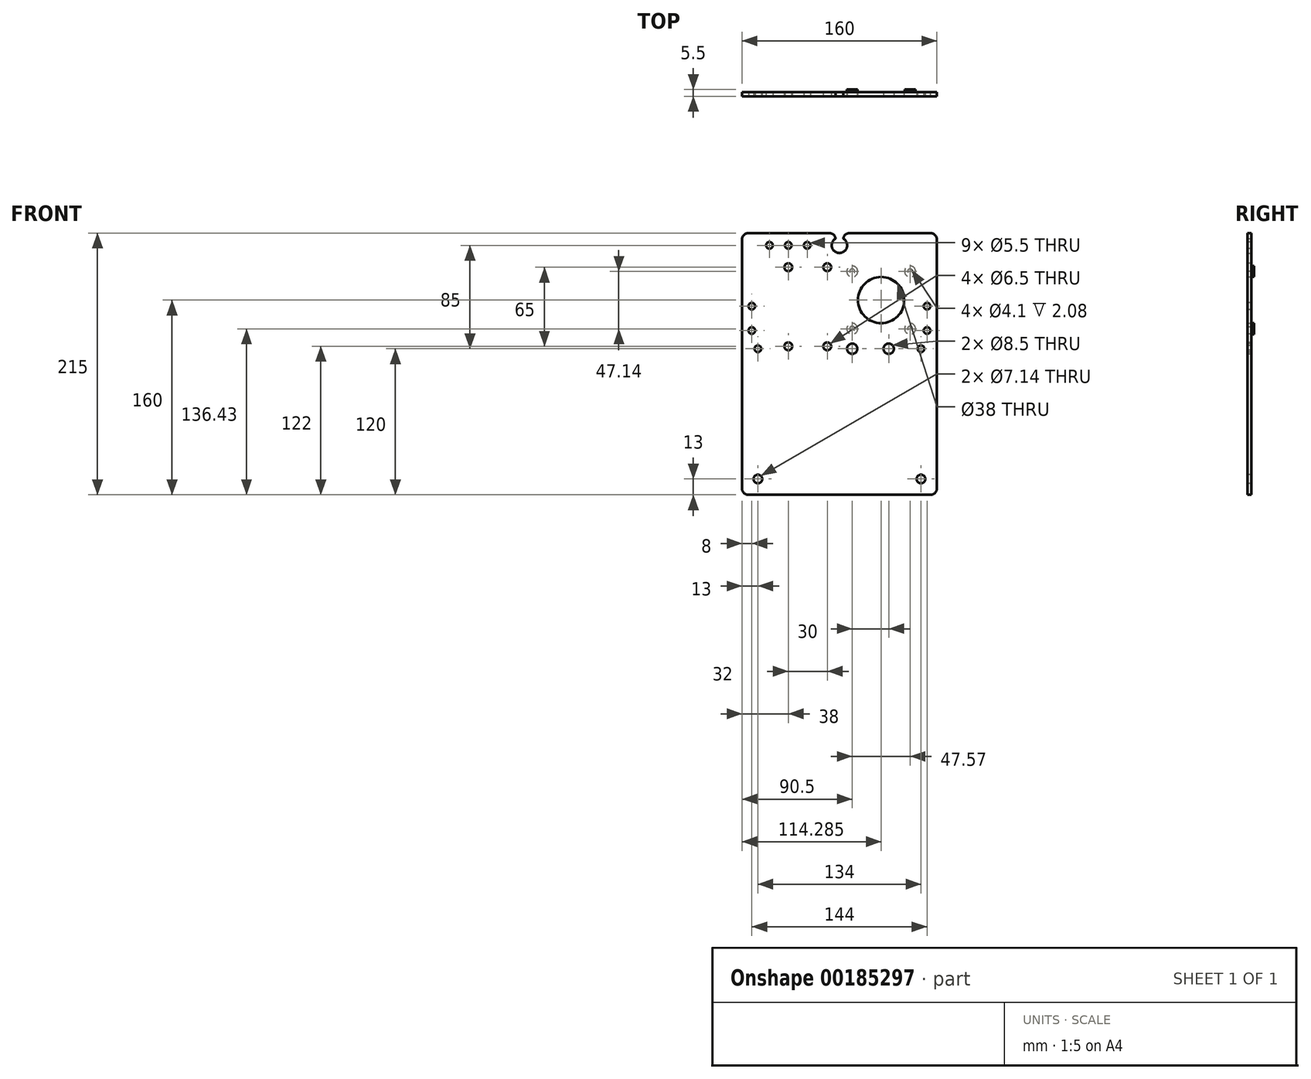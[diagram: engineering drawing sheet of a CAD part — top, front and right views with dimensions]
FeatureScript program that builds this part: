
annotation { "Feature Type Name" : "Feature", "Feature Type Description" : "" }
export const myFeature = defineFeature(function(context is Context, id is Id, definition is map)
    precondition{}
    {
        {
            var Q0;
            Q0=qCreatedBy(makeId("Front.planeOp"),FACE);
            var sketch = newSketch(context, id + "F0", { "sketchPlane" : qUnion([Q0])});
            skLineSegment(sketch, "E0.top", {"start": v(80, -107.5) * mm, "end": v(-80, -107.5) * mm});
            skLineSegment(sketch, "E0.right", {"start": v(-80, 107.5) * mm, "end": v(-80, -107.5) * mm});
            skPoint(sketch, "E0.middle", {"position": v(0, 0) * mm});
            skLineSegment(sketch, "E1", {"start": v(-80, 107.5) * mm, "end": v(-3.18, 107.5) * mm});
            skLineSegment(sketch, "E2", {"start": v(-3.18, 107.5) * mm, "end": v(-3.18, 103) * mm});
            skLineSegment(sketch, "E3", {"start": v(3.17, 103) * mm, "end": v(3.17, 107.5) * mm});
            skLineSegment(sketch, "E4", {"start": v(3.17, 107.5) * mm, "end": v(80, 107.5) * mm});
            skLineSegment(sketch, "E5", {"start": v(80, 107.5) * mm, "end": v(80, -107.5) * mm});
            skArc(sketch, "E6", {"start": v(-3.18, 103) * mm, "mid": v(0, 91.15) * mm, "end": v(3.17, 103) * mm});
            skLineSegment(sketch, "E7", {"start": v(7.75, 80.07) * mm, "end": v(7.75, 72.07) * mm, "construction": true});
            skLineSegment(sketch, "E8", {"start": v(13.25, 72.07) * mm, "end": v(13.25, 80.07) * mm, "construction": true});
            skLineSegment(sketch, "E9", {"start": v(55.32, 80.07) * mm, "end": v(55.32, 72.07) * mm, "construction": true});
            skLineSegment(sketch, "E10", {"start": v(60.82, 72.07) * mm, "end": v(60.82, 80.07) * mm, "construction": true});
            skLineSegment(sketch, "E11", {"start": v(60.82, 24.93) * mm, "end": v(60.82, 32.93) * mm, "construction": true});
            skLineSegment(sketch, "E12", {"start": v(55.32, 32.93) * mm, "end": v(55.32, 24.93) * mm, "construction": true});
            skLineSegment(sketch, "E13", {"start": v(13.25, 24.93) * mm, "end": v(13.25, 32.93) * mm, "construction": true});
            skLineSegment(sketch, "E14", {"start": v(7.75, 32.93) * mm, "end": v(7.75, 24.93) * mm, "construction": true});
            skLineSegment(sketch, "E15", {"start": v(7.75, 76.07) * mm, "end": v(13.25, 76.07) * mm, "construction": true});
            skLineSegment(sketch, "E16", {"start": v(55.32, 76.07) * mm, "end": v(60.82, 76.07) * mm, "construction": true});
            skLineSegment(sketch, "E17", {"start": v(55.32, 28.93) * mm, "end": v(60.82, 28.93) * mm, "construction": true});
            skLineSegment(sketch, "E18", {"start": v(13.25, 28.93) * mm, "end": v(7.75, 28.93) * mm, "construction": true});
            skPoint(sketch, "E18.endSnap0", {"position": v(7.75, 28.93) * mm});
            skLineSegment(sketch, "E19", {"start": v(10.5, 76.07) * mm, "end": v(10.5, 28.93) * mm, "construction": true});
            skLineSegment(sketch, "E20", {"start": v(10.5, 28.93) * mm, "end": v(58.07, 28.93) * mm, "construction": true});
            skLineSegment(sketch, "E21", {"start": v(58.07, 28.93) * mm, "end": v(58.07, 76.07) * mm, "construction": true});
            skLineSegment(sketch, "E22", {"start": v(58.07, 76.07) * mm, "end": v(10.5, 76.07) * mm, "construction": true});
            skArc(sketch, "E23", {"start": v(7.75, 80.07) * mm, "mid": v(10.5, 82.82) * mm, "end": v(13.25, 80.07) * mm, "construction": true});
            skArc(sketch, "E24", {"start": v(7.75, 72.07) * mm, "mid": v(10.5, 69.32) * mm, "end": v(13.25, 72.07) * mm, "construction": true});
            skArc(sketch, "E25", {"start": v(55.32, 80.07) * mm, "mid": v(58.07, 82.82) * mm, "end": v(60.82, 80.07) * mm, "construction": true});
            skArc(sketch, "E26", {"start": v(55.32, 72.07) * mm, "mid": v(58.07, 69.32) * mm, "end": v(60.82, 72.07) * mm, "construction": true});
            skArc(sketch, "E27", {"start": v(7.75, 32.93) * mm, "mid": v(10.5, 35.68) * mm, "end": v(13.25, 32.93) * mm, "construction": true});
            skArc(sketch, "E28", {"start": v(7.75, 24.93) * mm, "mid": v(10.5, 22.18) * mm, "end": v(13.25, 24.93) * mm, "construction": true});
            skArc(sketch, "E29", {"start": v(55.32, 32.93) * mm, "mid": v(58.07, 35.68) * mm, "end": v(60.82, 32.93) * mm, "construction": true});
            skArc(sketch, "E30", {"start": v(55.32, 24.93) * mm, "mid": v(58.07, 22.18) * mm, "end": v(60.82, 24.93) * mm, "construction": true});
            skCircle(sketch, "E31", {"center": v(34.29, 52.5) * mm, "radius": 19 * mm});
            skLineSegment(sketch, "E32", {"start": v(10.5, 52.5) * mm, "end": v(34.29, 52.5) * mm, "construction": true});
            skLineSegment(sketch, "E33", {"start": v(34.28, 52.5) * mm, "end": v(34.28, 76.07) * mm, "construction": true});
            skSolve(sketch);
        }
        {
            var Q0;
            Q0 = qSketchRegion(id + "F0", true);
            extrude(context, id + "F1", {"entities" : qUnion([Q0]), "depth" : 3.42 * mm});
        }
        {
            var Q0;
            Q0=makeQuery(id+"F1.opExtrude","SWEPT_EDGE",EDGE,{"disambiguationData":[OSD([sQuery(id+"F0.wireOp",EDGE,"E0.right"),sQuery(id+"F0.wireOp",EDGE,"E1")])]});
            var Q1;
            Q1=makeQuery(id+"F1.opExtrude","SWEPT_EDGE",EDGE,{"disambiguationData":[OSD([sQuery(id+"F0.wireOp",EDGE,"wBwmQqUi-94Xi-KIoa-cwVM-h10VN6lgfSyI"),sQuery(id+"F0.wireOp",EDGE,"E4")])]});
            var Q2;
            Q2=makeQuery(id+"F1.opExtrude","SWEPT_EDGE",EDGE,{"disambiguationData":[OSD([sQuery(id+"F0.wireOp",EDGE,"wBwmQqUi-94Xi-KIoa-cwVM-h10VN6lgfSyI"),sQuery(id+"F0.wireOp",EDGE,"zVrTCUyL-jB1j-ef0g-tJN7-1HJSPVF5DUSU")])]});
            var Q3;
            Q3=makeQuery(id+"F1.opExtrude","SWEPT_EDGE",EDGE,{"disambiguationData":[OSD([sQuery(id+"F0.wireOp",EDGE,"zVrTCUyL-jB1j-ef0g-tJN7-1HJSPVF5DUSU"),sQuery(id+"F0.wireOp",EDGE,"E5")])]});
            var Q4;
            Q4=makeQuery(id+"F1.opExtrude","SWEPT_EDGE",EDGE,{"disambiguationData":[OSD([sQuery(id+"F0.wireOp",EDGE,"E1"),sQuery(id+"F0.wireOp",EDGE,"E2")])]});
            var Q5;
            Q5=makeQuery(id+"F1.opExtrude","SWEPT_EDGE",EDGE,{"disambiguationData":[OSD([sQuery(id+"F0.wireOp",EDGE,"E3"),sQuery(id+"F0.wireOp",EDGE,"E4")])]});
            var Q6;
            Q6=makeQuery(id+"F1.opExtrude","SWEPT_EDGE",EDGE,{"disambiguationData":[OSD([sQuery(id+"F0.wireOp",EDGE,"E0.top"),sQuery(id+"F0.wireOp",EDGE,"E5")])]});
            var Q7;
            Q7=makeQuery(id+"F1.opExtrude","SWEPT_EDGE",EDGE,{"disambiguationData":[OSD([sQuery(id+"F0.wireOp",EDGE,"E0.top"),sQuery(id+"F0.wireOp",EDGE,"E0.right")])]});
            fillet(context, id + "F2", {"entities" : qUnion([Q0, Q1, Q2, Q3, Q4, Q5, Q6, Q7]), "radius" : 5 * mm, "tangentPropagation" : true, "allowEdgeOverflow" : false});
        }
        {
            var Q0;
            Q0=makeQuery(id+"F1.opExtrude","CAP_FACE",FACE,{"disambiguationData":[OSD([sQuery(id+"F0.wireOp",EDGE,"E0.top"),sQuery(id+"F0.wireOp",EDGE,"E0.right"),sQuery(id+"F0.wireOp",EDGE,"wBwmQqUi-94Xi-KIoa-cwVM-h10VN6lgfSyI"),sQuery(id+"F0.wireOp",EDGE,"zVrTCUyL-jB1j-ef0g-tJN7-1HJSPVF5DUSU"),sQuery(id+"F0.wireOp",EDGE,"E1"),sQuery(id+"F0.wireOp",EDGE,"E2"),sQuery(id+"F0.wireOp",EDGE,"E3"),sQuery(id+"F0.wireOp",EDGE,"E4"),sQuery(id+"F0.wireOp",EDGE,"E5"),sQuery(id+"F0.wireOp",EDGE,"E6"),sQuery(id+"F0.wireOp",EDGE,"E7"),sQuery(id+"F0.wireOp",EDGE,"E8"),sQuery(id+"F0.wireOp",EDGE,"E9"),sQuery(id+"F0.wireOp",EDGE,"E10"),sQuery(id+"F0.wireOp",EDGE,"E11"),sQuery(id+"F0.wireOp",EDGE,"E12"),sQuery(id+"F0.wireOp",EDGE,"E13"),sQuery(id+"F0.wireOp",EDGE,"E14"),sQuery(id+"F0.wireOp",EDGE,"E23"),sQuery(id+"F0.wireOp",EDGE,"E24"),sQuery(id+"F0.wireOp",EDGE,"E25"),sQuery(id+"F0.wireOp",EDGE,"E26"),sQuery(id+"F0.wireOp",EDGE,"E27"),sQuery(id+"F0.wireOp",EDGE,"E28"),sQuery(id+"F0.wireOp",EDGE,"E29"),sQuery(id+"F0.wireOp",EDGE,"E30")])],"isStart":false});
            var sketch = newSketch(context, id + "F3", { "sketchPlane" : qUnion([Q0])});
            skLineSegment(sketch, "E34", {"start": v(-42, 100) * mm, "end": v(-42, 95) * mm, "construction": true});
            skLineSegment(sketch, "E35", {"start": v(-57.5, 97.5) * mm, "end": v(-26.5, 97.5) * mm, "construction": true});
            skPoint(sketch, "E36", {"position": v(-42, 97.5) * mm});
            skLineSegment(sketch, "E37.bottom", {"start": v(-42, 79.5) * mm, "end": v(-10, 79.5) * mm, "construction": true});
            skLineSegment(sketch, "E37.top", {"start": v(-42, 14.5) * mm, "end": v(-10, 14.5) * mm, "construction": true});
            skLineSegment(sketch, "E37.left", {"start": v(-42, 79.5) * mm, "end": v(-42, 14.5) * mm, "construction": true});
            skLineSegment(sketch, "E37.right", {"start": v(-10, 79.5) * mm, "end": v(-10, 14.5) * mm, "construction": true});
            skLineSegment(sketch, "E38.bottom", {"start": v(-72, 47.5) * mm, "end": v(72, 47.5) * mm, "construction": true});
            skLineSegment(sketch, "E38.top", {"start": v(-72, 27.5) * mm, "end": v(72, 27.5) * mm, "construction": true});
            skLineSegment(sketch, "E38.left", {"start": v(-72, 47.5) * mm, "end": v(-72, 27.5) * mm, "construction": true});
            skLineSegment(sketch, "E38.right", {"start": v(72, 47.5) * mm, "end": v(72, 27.5) * mm, "construction": true});
            skLineSegment(sketch, "E39", {"start": v(10.5, 12.5) * mm, "end": v(40.5, 12.5) * mm, "construction": true});
            skLineSegment(sketch, "E40", {"start": v(-67, -94.5) * mm, "end": v(67, -94.5) * mm, "construction": true});
            skLineSegment(sketch, "E41", {"start": v(10.5, 12.5) * mm, "end": v(-67, 12.5) * mm, "construction": true});
            skLineSegment(sketch, "E42", {"start": v(40.5, 12.5) * mm, "end": v(67, 12.5) * mm, "construction": true});
            skLineSegment(sketch, "E43", {"start": v(67, 12.5) * mm, "end": v(67, -94.5) * mm, "construction": true});
            skSolve(sketch);
        }
        {
            var Q0;
            Q0=sQuery(id+"F3.wireOp",VERTEX,"E37.left.start");
            var Q1;
            Q1=sQuery(id+"F3.wireOp",VERTEX,"E37.right.start");
            var Q2;
            Q2=sQuery(id+"F3.wireOp",VERTEX,"E37.left.end");
            var Q3;
            Q3=sQuery(id+"F3.wireOp",VERTEX,"E37.right.end");
            var Q4;
            Q4=makeQuery(id+"F1.opExtrude","SWEPT_BODY",BODY,{"disambiguationData":[OSD([sQuery(id+"F0.wireOp",EDGE,"E0.top"),sQuery(id+"F0.wireOp",EDGE,"E0.right"),sQuery(id+"F0.wireOp",EDGE,"wBwmQqUi-94Xi-KIoa-cwVM-h10VN6lgfSyI"),sQuery(id+"F0.wireOp",EDGE,"zVrTCUyL-jB1j-ef0g-tJN7-1HJSPVF5DUSU"),sQuery(id+"F0.wireOp",EDGE,"E1"),sQuery(id+"F0.wireOp",EDGE,"E2"),sQuery(id+"F0.wireOp",EDGE,"E3"),sQuery(id+"F0.wireOp",EDGE,"E4"),sQuery(id+"F0.wireOp",EDGE,"E5"),sQuery(id+"F0.wireOp",EDGE,"E6"),sQuery(id+"F0.wireOp",EDGE,"E7"),sQuery(id+"F0.wireOp",EDGE,"E8"),sQuery(id+"F0.wireOp",EDGE,"E9"),sQuery(id+"F0.wireOp",EDGE,"E10"),sQuery(id+"F0.wireOp",EDGE,"E11"),sQuery(id+"F0.wireOp",EDGE,"E12"),sQuery(id+"F0.wireOp",EDGE,"E13"),sQuery(id+"F0.wireOp",EDGE,"E14"),sQuery(id+"F0.wireOp",EDGE,"E23"),sQuery(id+"F0.wireOp",EDGE,"E24"),sQuery(id+"F0.wireOp",EDGE,"E25"),sQuery(id+"F0.wireOp",EDGE,"E26"),sQuery(id+"F0.wireOp",EDGE,"E27"),sQuery(id+"F0.wireOp",EDGE,"E28"),sQuery(id+"F0.wireOp",EDGE,"E29"),sQuery(id+"F0.wireOp",EDGE,"E30")])]});
            hole(context, id + "F4", {"style" : HoleStyle.SIMPLE, "endStyle" : HoleEndStyle.THROUGH, "holeDiameter" : 6.5 * mm, "locations" : qUnion([Q0, Q1, Q2, Q3]), "scope" : qUnion([Q4]), "isTappedThrough" : true});
        }
        {
            var Q0;
            Q0=sQuery(id+"F3.wireOp",VERTEX,"E38.bottom.start");
            var Q1;
            Q1=sQuery(id+"F3.wireOp",VERTEX,"E38.left.end");
            var Q2;
            Q2=sQuery(id+"F3.wireOp",VERTEX,"E38.right.start");
            var Q3;
            Q3=sQuery(id+"F3.wireOp",VERTEX,"E38.top.end");
            var Q4;
            Q4=sQuery(id+"F3.wireOp",VERTEX,"E35.start");
            var Q5;
            Q5=sQuery(id+"F3.wireOp",VERTEX,"E35.end");
            var Q6;
            Q6=sQuery(id+"F3.wireOp",VERTEX,"E41.end");
            var Q7;
            Q7=sQuery(id+"F3.wireOp",VERTEX,"E43.start");
            var Q8;
            Q8=sQuery(id+"F3.wireOp",VERTEX,"E36");
            var Q9;
            Q9=makeQuery(id+"F1.opExtrude","SWEPT_BODY",BODY,{"disambiguationData":[OSD([sQuery(id+"F0.wireOp",EDGE,"E0.top"),sQuery(id+"F0.wireOp",EDGE,"E0.right"),sQuery(id+"F0.wireOp",EDGE,"wBwmQqUi-94Xi-KIoa-cwVM-h10VN6lgfSyI"),sQuery(id+"F0.wireOp",EDGE,"zVrTCUyL-jB1j-ef0g-tJN7-1HJSPVF5DUSU"),sQuery(id+"F0.wireOp",EDGE,"E1"),sQuery(id+"F0.wireOp",EDGE,"E2"),sQuery(id+"F0.wireOp",EDGE,"E3"),sQuery(id+"F0.wireOp",EDGE,"E4"),sQuery(id+"F0.wireOp",EDGE,"E5"),sQuery(id+"F0.wireOp",EDGE,"E6"),sQuery(id+"F0.wireOp",EDGE,"E7"),sQuery(id+"F0.wireOp",EDGE,"E8"),sQuery(id+"F0.wireOp",EDGE,"E9"),sQuery(id+"F0.wireOp",EDGE,"E10"),sQuery(id+"F0.wireOp",EDGE,"E11"),sQuery(id+"F0.wireOp",EDGE,"E12"),sQuery(id+"F0.wireOp",EDGE,"E13"),sQuery(id+"F0.wireOp",EDGE,"E14"),sQuery(id+"F0.wireOp",EDGE,"E23"),sQuery(id+"F0.wireOp",EDGE,"E24"),sQuery(id+"F0.wireOp",EDGE,"E25"),sQuery(id+"F0.wireOp",EDGE,"E26"),sQuery(id+"F0.wireOp",EDGE,"E27"),sQuery(id+"F0.wireOp",EDGE,"E28"),sQuery(id+"F0.wireOp",EDGE,"E29"),sQuery(id+"F0.wireOp",EDGE,"E30")])]});
            hole(context, id + "F5", {"style" : HoleStyle.SIMPLE, "endStyle" : HoleEndStyle.THROUGH, "holeDiameter" : 5.5 * mm, "locations" : qUnion([Q0, Q1, Q2, Q3, Q4, Q5, Q6, Q7, Q8]), "scope" : qUnion([Q9]), "isTappedThrough" : true});
        }
        {
            var Q0;
            Q0=sQuery(id+"F3.wireOp",VERTEX,"E39.start");
            var Q1;
            Q1=sQuery(id+"F3.wireOp",VERTEX,"E42.start");
            var Q2;
            Q2=makeQuery(id+"F1.opExtrude","SWEPT_BODY",BODY,{"disambiguationData":[OSD([sQuery(id+"F0.wireOp",EDGE,"E0.top"),sQuery(id+"F0.wireOp",EDGE,"E0.right"),sQuery(id+"F0.wireOp",EDGE,"wBwmQqUi-94Xi-KIoa-cwVM-h10VN6lgfSyI"),sQuery(id+"F0.wireOp",EDGE,"zVrTCUyL-jB1j-ef0g-tJN7-1HJSPVF5DUSU"),sQuery(id+"F0.wireOp",EDGE,"E1"),sQuery(id+"F0.wireOp",EDGE,"E2"),sQuery(id+"F0.wireOp",EDGE,"E3"),sQuery(id+"F0.wireOp",EDGE,"E4"),sQuery(id+"F0.wireOp",EDGE,"E5"),sQuery(id+"F0.wireOp",EDGE,"E6"),sQuery(id+"F0.wireOp",EDGE,"E7"),sQuery(id+"F0.wireOp",EDGE,"E8"),sQuery(id+"F0.wireOp",EDGE,"E9"),sQuery(id+"F0.wireOp",EDGE,"E10"),sQuery(id+"F0.wireOp",EDGE,"E11"),sQuery(id+"F0.wireOp",EDGE,"E12"),sQuery(id+"F0.wireOp",EDGE,"E13"),sQuery(id+"F0.wireOp",EDGE,"E14"),sQuery(id+"F0.wireOp",EDGE,"E23"),sQuery(id+"F0.wireOp",EDGE,"E24"),sQuery(id+"F0.wireOp",EDGE,"E25"),sQuery(id+"F0.wireOp",EDGE,"E26"),sQuery(id+"F0.wireOp",EDGE,"E27"),sQuery(id+"F0.wireOp",EDGE,"E28"),sQuery(id+"F0.wireOp",EDGE,"E29"),sQuery(id+"F0.wireOp",EDGE,"E30")])]});
            hole(context, id + "F6", {"style" : HoleStyle.SIMPLE, "endStyle" : HoleEndStyle.THROUGH, "holeDiameter" : 8.5 * mm, "locations" : qUnion([Q0, Q1]), "scope" : qUnion([Q2]), "isTappedThrough" : true});
        }
        {
            var Q0;
            Q0=sQuery(id+"F3.wireOp",VERTEX,"E40.start");
            var Q1;
            Q1=sQuery(id+"F3.wireOp",VERTEX,"E43.end");
            var Q2;
            Q2=makeQuery(id+"F1.opExtrude","SWEPT_BODY",BODY,{"disambiguationData":[OSD([sQuery(id+"F0.wireOp",EDGE,"E0.top"),sQuery(id+"F0.wireOp",EDGE,"E0.right"),sQuery(id+"F0.wireOp",EDGE,"wBwmQqUi-94Xi-KIoa-cwVM-h10VN6lgfSyI"),sQuery(id+"F0.wireOp",EDGE,"zVrTCUyL-jB1j-ef0g-tJN7-1HJSPVF5DUSU"),sQuery(id+"F0.wireOp",EDGE,"E1"),sQuery(id+"F0.wireOp",EDGE,"E2"),sQuery(id+"F0.wireOp",EDGE,"E3"),sQuery(id+"F0.wireOp",EDGE,"E4"),sQuery(id+"F0.wireOp",EDGE,"E5"),sQuery(id+"F0.wireOp",EDGE,"E6"),sQuery(id+"F0.wireOp",EDGE,"E7"),sQuery(id+"F0.wireOp",EDGE,"E8"),sQuery(id+"F0.wireOp",EDGE,"E9"),sQuery(id+"F0.wireOp",EDGE,"E10"),sQuery(id+"F0.wireOp",EDGE,"E11"),sQuery(id+"F0.wireOp",EDGE,"E12"),sQuery(id+"F0.wireOp",EDGE,"E13"),sQuery(id+"F0.wireOp",EDGE,"E14"),sQuery(id+"F0.wireOp",EDGE,"E23"),sQuery(id+"F0.wireOp",EDGE,"E24"),sQuery(id+"F0.wireOp",EDGE,"E25"),sQuery(id+"F0.wireOp",EDGE,"E26"),sQuery(id+"F0.wireOp",EDGE,"E27"),sQuery(id+"F0.wireOp",EDGE,"E28"),sQuery(id+"F0.wireOp",EDGE,"E29"),sQuery(id+"F0.wireOp",EDGE,"E30")])]});
            hole(context, id + "F7", {"style" : HoleStyle.SIMPLE, "endStyle" : HoleEndStyle.THROUGH, "holeDiameter" : 7.14 * mm, "locations" : qUnion([Q0, Q1]), "scope" : qUnion([Q2]), "isTappedThrough" : true});
        }
        {
            var Q0;
            Q0=makeQuery(id+"F1.opExtrude","CAP_FACE",FACE,{"disambiguationData":[OSD([sQuery(id+"F0.wireOp",EDGE,"E0.top"),sQuery(id+"F0.wireOp",EDGE,"E0.right"),sQuery(id+"F0.wireOp",EDGE,"E1"),sQuery(id+"F0.wireOp",EDGE,"E2"),sQuery(id+"F0.wireOp",EDGE,"E3"),sQuery(id+"F0.wireOp",EDGE,"E4"),sQuery(id+"F0.wireOp",EDGE,"E5"),sQuery(id+"F0.wireOp",EDGE,"E6"),sQuery(id+"F0.wireOp",EDGE,"E31")])],"isStart":false});
            var sketch = newSketch(context, id + "F8", { "sketchPlane" : qUnion([Q0])});
            skCircle(sketch, "E44", {"center": v(10.5, 76.07) * mm, "radius": 4.5 * mm});
            skCircle(sketch, "E45", {"center": v(58.07, 76.07) * mm, "radius": 4.5 * mm});
            skCircle(sketch, "E46", {"center": v(58.07, 28.93) * mm, "radius": 4.5 * mm});
            skCircle(sketch, "E47", {"center": v(10.5, 28.93) * mm, "radius": 4.5 * mm});
            skSolve(sketch);
        }
        {
            var Q0;
            Q0 = qSketchRegion(id + "F8", true);
            extrude(context, id + "F9", {"entities" : qUnion([Q0]), "operationType" : NewBodyOperationType.ADD, "oppositeDirection" : true, "depth" : 5.5 * mm});
        }
        {
            var Q0;
            Q0=sQuery(id+"F0.wireOp",VERTEX,"E22.end");
            var Q1;
            Q1=sQuery(id+"F0.wireOp",VERTEX,"E21.end");
            var Q2;
            Q2=sQuery(id+"F0.wireOp",VERTEX,"E19.end");
            var Q3;
            Q3=sQuery(id+"F0.wireOp",VERTEX,"E20.end");
            var Q4;
            Q4=makeQuery(id+"F1.opExtrude","SWEPT_BODY",BODY,{"disambiguationData":[OSD([sQuery(id+"F0.wireOp",EDGE,"E0.top"),sQuery(id+"F0.wireOp",EDGE,"E0.right"),sQuery(id+"F0.wireOp",EDGE,"E1"),sQuery(id+"F0.wireOp",EDGE,"E2"),sQuery(id+"F0.wireOp",EDGE,"E3"),sQuery(id+"F0.wireOp",EDGE,"E4"),sQuery(id+"F0.wireOp",EDGE,"E5"),sQuery(id+"F0.wireOp",EDGE,"E6"),sQuery(id+"F0.wireOp",EDGE,"E31")])]});
            hole(context, id + "F10", {"style" : HoleStyle.SIMPLE, "endStyle" : HoleEndStyle.THROUGH, "standardTappedOrClearance" : lookupTablePath({ "standard" : "ISO", "engagement" : "75%", "pitch" : "0.9 mm", "size" : "M5", "type" : "Tapped" }), "standardBlindInLast" : lookupTablePath({ "standard" : "ISO", "engagement" : "75%", "pitch" : "0.9 mm", "size" : "M5", "type" : "Tapped" }), "holeDiameter" : 4.1 * mm, "locations" : qUnion([Q0, Q1, Q2, Q3]), "scope" : qUnion([Q4]), "isTappedThrough" : true, "showTappedDepth" : true});
        }
    });
